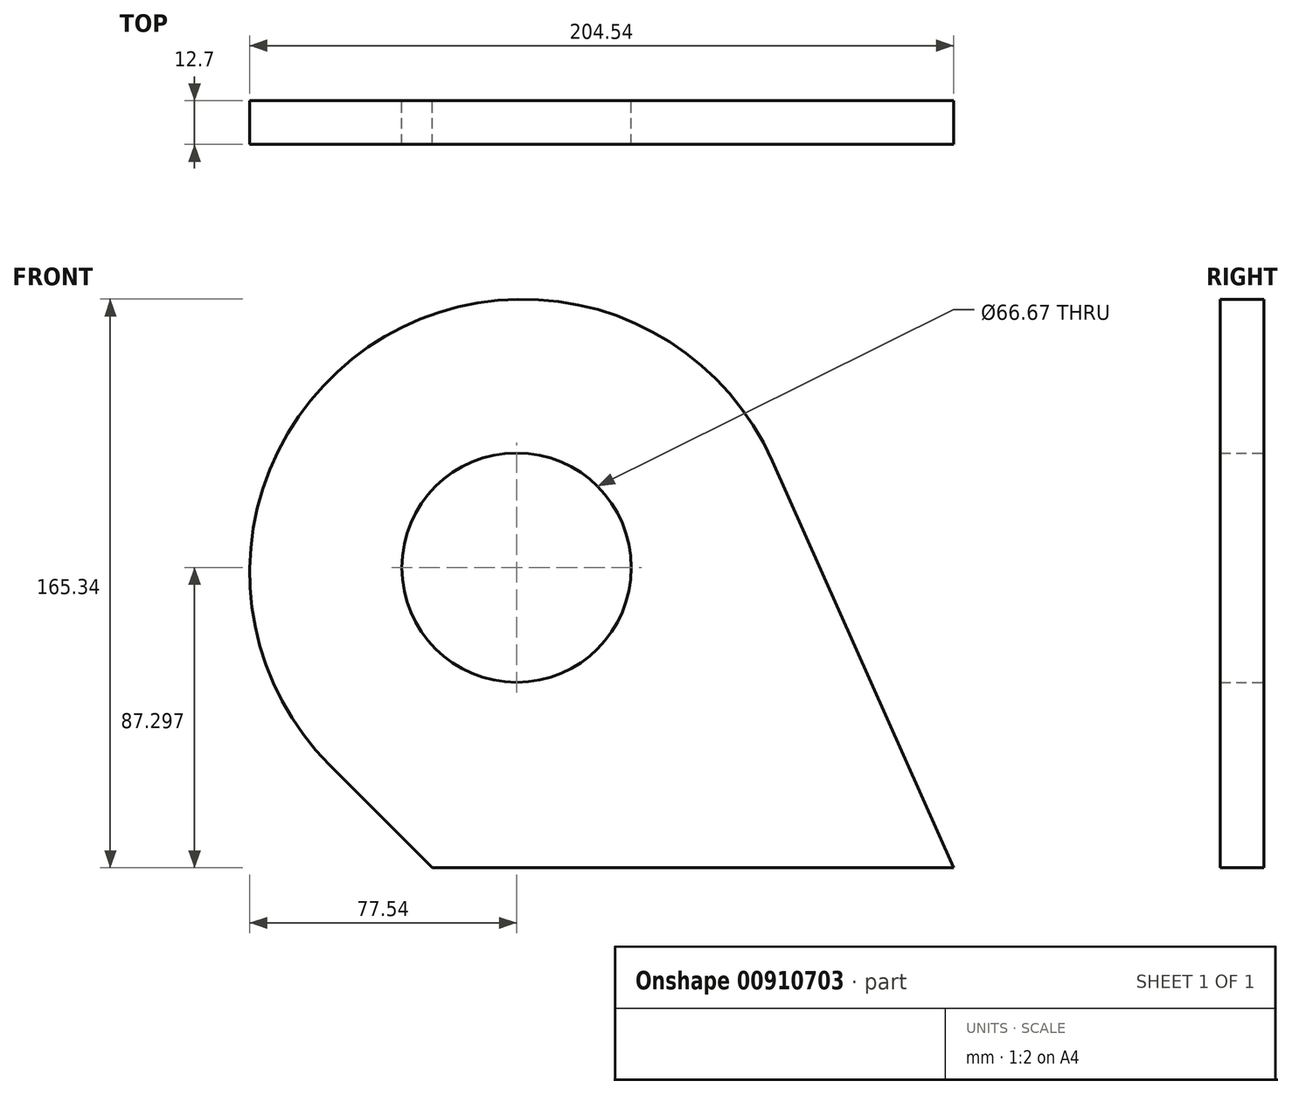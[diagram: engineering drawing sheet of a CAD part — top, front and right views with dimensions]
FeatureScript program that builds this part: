
annotation { "Feature Type Name" : "Feature", "Feature Type Description" : "" }
export const myFeature = defineFeature(function(context is Context, id is Id, definition is map)
    precondition{}
    {
        {
            var Q0;
            Q0=qCreatedBy(makeId("Front.planeOp"),FACE);
            var sketch = newSketch(context, id + "F0", { "sketchPlane" : qUnion([Q0])});
            skArc(sketch, "E0", {"start": v(72.51, 32.28) * mm, "mid": v(-44.96, 65.42) * mm, "end": v(-56.13, -56.13) * mm});
            skCircle(sketch, "E1", {"center": v(-1.84, 1.34) * mm, "radius": 33.34 * mm});
            skLineSegment(sketch, "E2", {"start": v(-26.3, -85.96) * mm, "end": v(125.16, -85.96) * mm});
            skLineSegment(sketch, "E3", {"start": v(125.16, -85.96) * mm, "end": v(72.51, 32.28) * mm});
            skLineSegment(sketch, "E4", {"start": v(-26.3, -85.96) * mm, "end": v(-56.13, -56.13) * mm});
            skSolve(sketch);
        }
        {
            var Q0;
            Q0=makeQuery(id+"F0.imprint","IMPRINT",FACE,{"disambiguationData":[TD([[makeQuery(id+"F0.imprint","IMPRINT",EDGE,{"derivedFrom":sQuery(id+"F0.wireOp",EDGE,"E0")}),1.0]])]});
            extrude(context, id + "F1", {"entities" : qUnion([Q0]), "depth" : 12.7 * mm, "offsetDistance" : 25.4 * mm});
        }
    });
